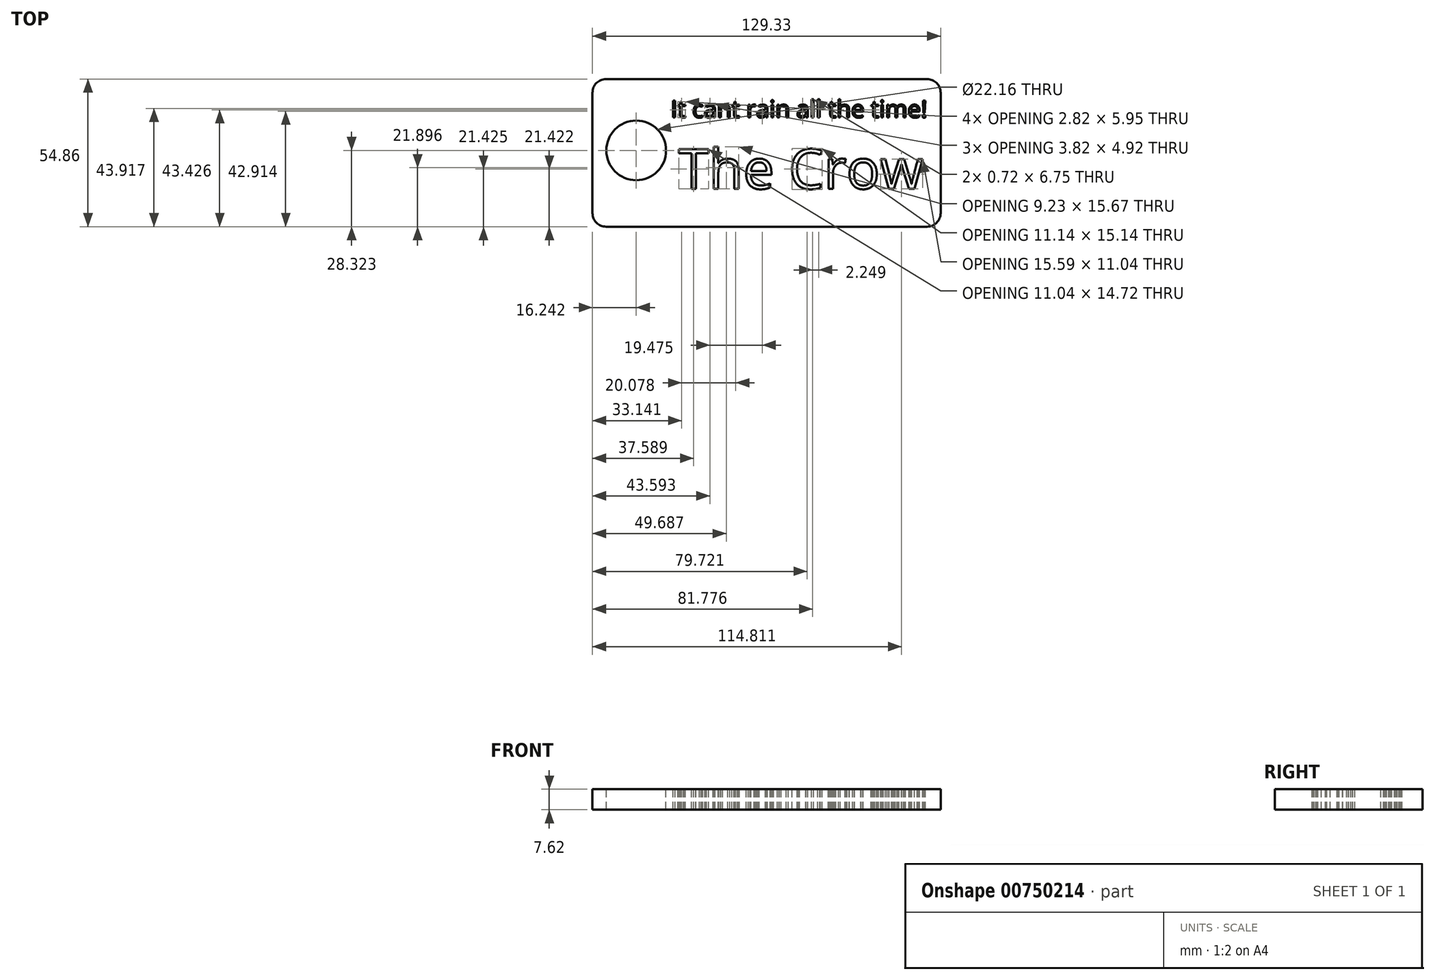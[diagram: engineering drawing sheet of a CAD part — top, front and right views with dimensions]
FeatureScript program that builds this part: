
annotation { "Feature Type Name" : "Feature", "Feature Type Description" : "" }
export const myFeature = defineFeature(function(context is Context, id is Id, definition is map)
    precondition{}
    {
        {
            var Q0;
            Q0=qCreatedBy(makeId("Top.planeOp"),FACE);
            var sketch = newSketch(context, id + "F0", { "sketchPlane" : qUnion([Q0])});
            skLineSegment(sketch, "E0.bottom", {"start": v(-64.07, 35.35) * mm, "end": v(65.26, 35.35) * mm});
            skLineSegment(sketch, "E0.top", {"start": v(-64.07, -19.5) * mm, "end": v(65.26, -19.5) * mm});
            skLineSegment(sketch, "E0.left", {"start": v(-64.07, 35.35) * mm, "end": v(-64.07, -19.5) * mm});
            skLineSegment(sketch, "E0.right", {"start": v(65.26, 35.35) * mm, "end": v(65.26, -19.5) * mm});
            skSolve(sketch);
        }
        {
            var Q0;
            Q0=makeQuery(id+"F0.imprint","IMPRINT",FACE,{"disambiguationData":[TD([[makeQuery(id+"F0.imprint","IMPRINT",EDGE,{"derivedFrom":sQuery(id+"F0.wireOp",EDGE,"E0.bottom")}),-1.0]])]});
            extrude(context, id + "F1", {"entities" : qUnion([Q0]), "depth" : 7.62 * mm, "offsetDistance" : 25.4 * mm});
        }
        {
            var Q0;
            Q0=makeQuery(id+"F1.opExtrude","CAP_FACE",FACE,{"disambiguationData":[OSD([sQuery(id+"F0.wireOp",EDGE,"E0.bottom"),sQuery(id+"F0.wireOp",EDGE,"E0.top"),sQuery(id+"F0.wireOp",EDGE,"E0.left"),sQuery(id+"F0.wireOp",EDGE,"E0.right")])],"isStart":false});
            var sketch = newSketch(context, id + "F2", { "sketchPlane" : qUnion([Q0])});
            skCircle(sketch, "E1", {"center": v(-47.83, 8.81) * mm, "radius": 11.08 * mm});
            skSolve(sketch);
        }
        {
            var Q0;
            Q0=makeQuery(id+"F2.imprint","IMPRINT",FACE,{"disambiguationData":[TD([[makeQuery(id+"F2.imprint","IMPRINT",EDGE,{"derivedFrom":sQuery(id+"F2.wireOp",EDGE,"E1")}),1.0]])]});
            extrude(context, id + "F3", {"entities" : qUnion([Q0]), "operationType" : NewBodyOperationType.REMOVE, "oppositeDirection" : true, "depth" : 25.4 * mm, "offsetDistance" : 25.4 * mm});
        }
        {
            var Q0;
            Q0=makeQuery(id+"F1.opExtrude","SWEPT_EDGE",EDGE,{"disambiguationData":[OSD([sQuery(id+"F0.wireOp",EDGE,"E0.top"),sQuery(id+"F0.wireOp",EDGE,"E0.right")])]});
            fillet(context, id + "F4", {"entities" : qUnion([Q0]), "radius" : 5.08 * mm, "tangentPropagation" : true, "allowEdgeOverflow" : false});
        }
        {
            var Q0;
            Q0=makeQuery(id+"F1.opExtrude","SWEPT_EDGE",EDGE,{"disambiguationData":[OSD([sQuery(id+"F0.wireOp",EDGE,"E0.bottom"),sQuery(id+"F0.wireOp",EDGE,"E0.right")])]});
            fillet(context, id + "F5", {"entities" : qUnion([Q0]), "radius" : 5.08 * mm, "tangentPropagation" : true, "allowEdgeOverflow" : false});
        }
        {
            var Q0;
            Q0=makeQuery(id+"F1.opExtrude","SWEPT_EDGE",EDGE,{"disambiguationData":[OSD([sQuery(id+"F0.wireOp",EDGE,"E0.bottom"),sQuery(id+"F0.wireOp",EDGE,"E0.left")])]});
            var Q1;
            Q1=makeQuery(id+"F1.opExtrude","SWEPT_EDGE",EDGE,{"disambiguationData":[OSD([sQuery(id+"F0.wireOp",EDGE,"E0.top"),sQuery(id+"F0.wireOp",EDGE,"E0.left")])]});
            fillet(context, id + "F6", {"entities" : qUnion([Q0, Q1]), "radius" : 5.08 * mm, "tangentPropagation" : true, "allowEdgeOverflow" : false});
        }
        {
            var Q0;
            Q0=makeQuery(id+"F1.opExtrude","CAP_FACE",FACE,{"disambiguationData":[OSD([sQuery(id+"F0.wireOp",EDGE,"E0.bottom"),sQuery(id+"F0.wireOp",EDGE,"E0.top"),sQuery(id+"F0.wireOp",EDGE,"E0.left"),sQuery(id+"F0.wireOp",EDGE,"E0.right")])],"isStart":false});
            var sketch = newSketch(context, id + "F7", { "sketchPlane" : qUnion([Q0])});
            skText(sketch, "E2", { "text": "It cant rain all the time!", "fontName": "OpenSans-Regular.ttf"});
            const initialGuessF7  = {"E2": [-0.03495, 0.02103, 1, 0, 0.0064]};
            skSetInitialGuess(sketch, initialGuessF7);
            skSolve(sketch);
        }
        {
            var Q0;
            Q0=makeQuery(id+"F7.imprint","IMPRINT",FACE,{"disambiguationData":[TD([[makeQuery(id+"F7.imprint","IMPRINT",EDGE,{"derivedFrom":sQuery(id+"F7.wireOp",EDGE,"E2.sketch_text.stroke-0")}),1.0]])]});
            var sketch = newSketch(context, id + "F8", { "sketchPlane" : qUnion([Q0])});
            skText(sketch, "E3", { "text": "The Crow", "fontName": "OpenSans-Regular.ttf"});
            const initialGuessF8  = {"E3": [-0.03218, -0.00545, 1, 0, 0.01485]};
            skSetInitialGuess(sketch, initialGuessF8);
            skSolve(sketch);
        }
        {
            var Q0;
            Q0 = qSketchRegion(id + "F7", true);
            extrude(context, id + "F9", {"entities" : qUnion([Q0]), "operationType" : NewBodyOperationType.REMOVE, "oppositeDirection" : true, "depth" : 25.4 * mm, "offsetDistance" : 25.4 * mm});
        }
        {
            var Q0;
            Q0 = qSketchRegion(id + "F8", true);
            extrude(context, id + "F10", {"entities" : qUnion([Q0]), "operationType" : NewBodyOperationType.REMOVE, "oppositeDirection" : true, "depth" : 25.4 * mm, "offsetDistance" : 25.4 * mm});
        }
    });
